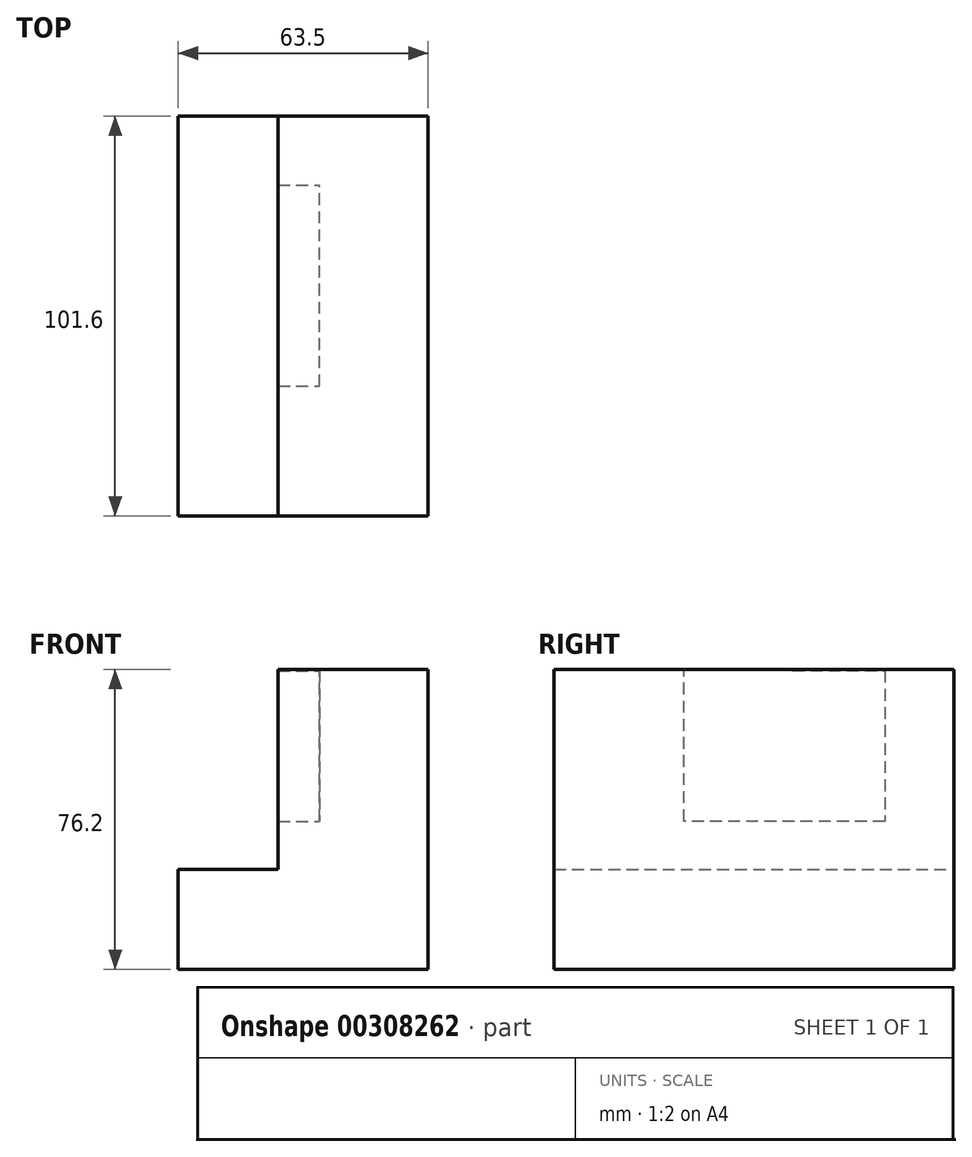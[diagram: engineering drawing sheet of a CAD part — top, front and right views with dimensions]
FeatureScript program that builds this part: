
annotation { "Feature Type Name" : "Feature", "Feature Type Description" : "" }
export const myFeature = defineFeature(function(context is Context, id is Id, definition is map)
    precondition{}
    {
        {
            var Q0;
            Q0=qCreatedBy(makeId("Front.planeOp"),FACE);
            var sketch = newSketch(context, id + "F0", { "sketchPlane" : qUnion([Q0])});
            skLineSegment(sketch, "E0", {"start": v(-35.89, -18.68) * mm, "end": v(27.61, -18.68) * mm});
            skLineSegment(sketch, "E1", {"start": v(27.61, -18.68) * mm, "end": v(27.61, 57.52) * mm});
            skLineSegment(sketch, "E2", {"start": v(27.61, 57.52) * mm, "end": v(-10.49, 57.52) * mm});
            skLineSegment(sketch, "E3", {"start": v(-10.49, 57.52) * mm, "end": v(-10.49, 6.72) * mm});
            skLineSegment(sketch, "E4", {"start": v(-10.49, 6.72) * mm, "end": v(-35.89, 6.72) * mm});
            skLineSegment(sketch, "E5", {"start": v(-35.89, 6.72) * mm, "end": v(-35.89, -18.68) * mm});
            skSolve(sketch);
        }
        {
            var Q0;
            Q0 = qSketchRegion(id + "F0", true);
            extrude(context, id + "F1", {"entities" : qUnion([Q0]), "depth" : 101.6 * mm});
        }
        {
            var Q0;
            Q0=qCreatedBy(makeId("Right.planeOp"),FACE);
            var sketch = newSketch(context, id + "F2", { "sketchPlane" : qUnion([Q0])});
            skLineSegment(sketch, "E6", {"start": v(-17.55, 57.2) * mm, "end": v(-17.55, 18.97) * mm});
            skLineSegment(sketch, "E7", {"start": v(-17.55, 18.97) * mm, "end": v(-68.6, 18.97) * mm});
            skLineSegment(sketch, "E8", {"start": v(-68.6, 18.97) * mm, "end": v(-68.6, 57.48) * mm});
            skLineSegment(sketch, "E9", {"start": v(-68.6, 57.48) * mm, "end": v(-17.55, 57.2) * mm});
            skSolve(sketch);
        }
        {
            var Q0;
            Q0 = qSketchRegion(id + "F2", true);
            extrude(context, id + "F3", {"entities" : qUnion([Q0]), "operationType" : NewBodyOperationType.REMOVE, "oppositeDirection" : true, "depth" : 25.4 * mm});
        }
    });
